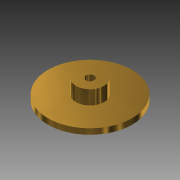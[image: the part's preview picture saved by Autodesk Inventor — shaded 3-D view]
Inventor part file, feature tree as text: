
AUTODESK INVENTOR PART (.ipt)
format: ipt  version: 2015 (Build 190159000, 159)  size: 114,688 bytes
history: native  units: mm
features: extrude x4, sketch x4, other x2
ambient origin geometry x8: Origin, YZ Plane, XZ Plane, XY Plane, X Axis, Y Axis, Z Axis, Center Point
bodies: Body1 (feature_tree)
feature tree (10):
  other  "Gear2_S50B 60B+0203"
  other  "ソリッド1"
  extrude  "押し出し1"  Depth=30.0mm
  extrude  "押し出し2"  Depth=2.0mm TaperAngle=0.0deg
  extrude  "押し出し4"  Depth=10.0mm
  extrude  "押し出し5"  Depth=5.0mm TaperAngle=0.0deg
  sketch  "スケッチ1"
  sketch  "スケッチ2"
  sketch  "スケッチ4"
  sketch  "スケッチ5"
